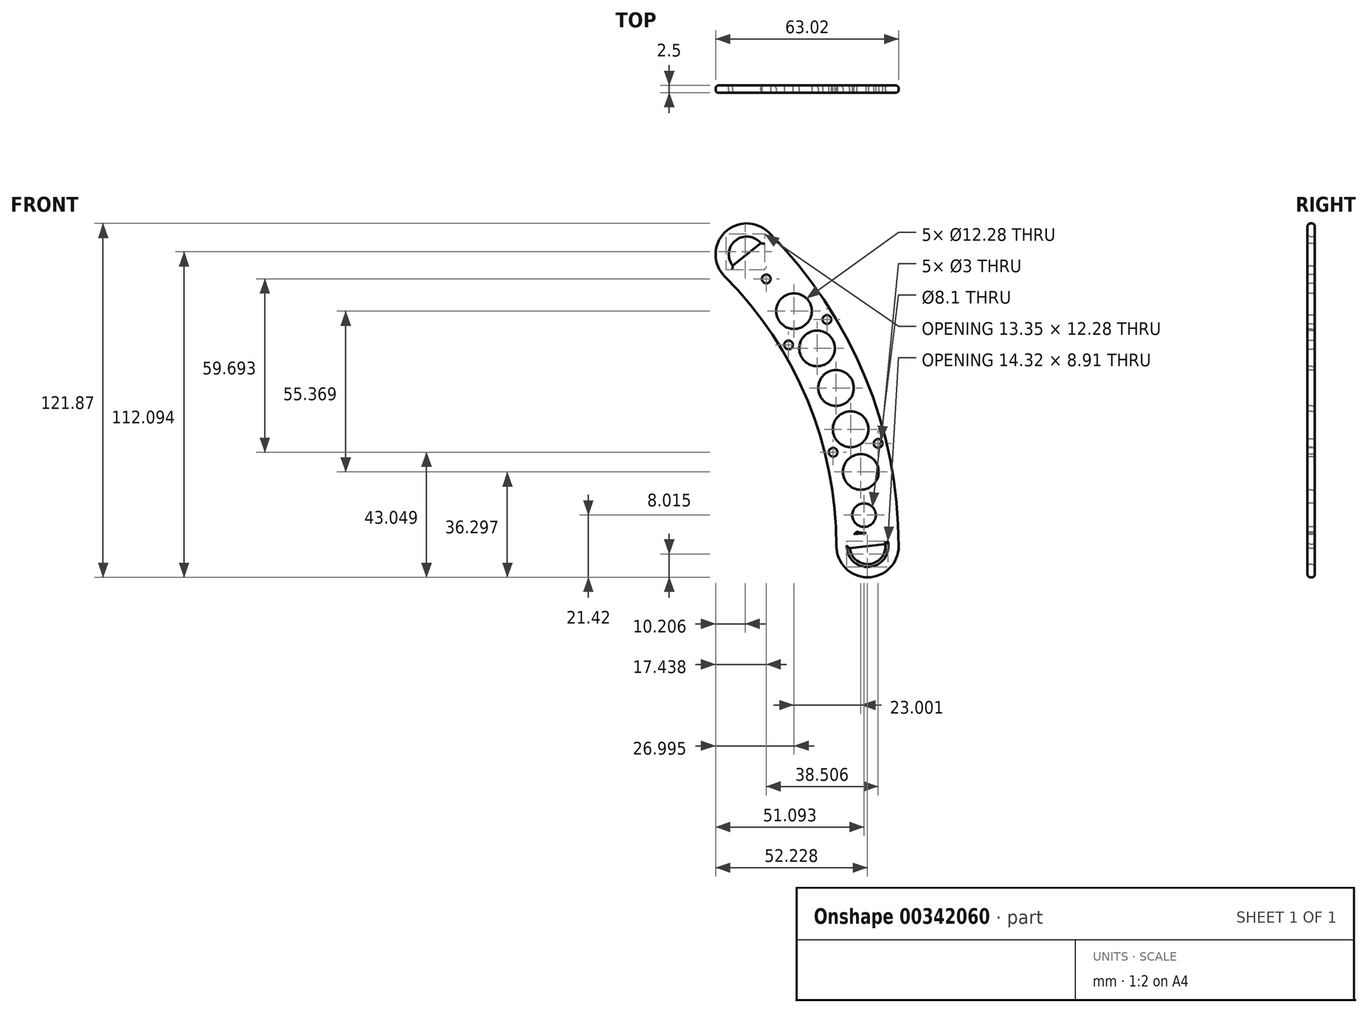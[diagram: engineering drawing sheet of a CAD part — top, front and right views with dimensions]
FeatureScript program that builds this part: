
annotation { "Feature Type Name" : "Feature", "Feature Type Description" : "" }
export const myFeature = defineFeature(function(context is Context, id is Id, definition is map)
    precondition{}
    {
        {
            var Q0;
            Q0=qCreatedBy(makeId("Front.planeOp"),FACE);
            var sketch = newSketch(context, id + "F0", { "sketchPlane" : qUnion([Q0])});
            skCircle(sketch, "E0", {"center": v(0, 0) * mm, "radius": 152.8 * mm});
            skCircle(sketch, "E1", {"center": v(0, 0) * mm, "radius": 131.4 * mm});
            skLineSegment(sketch, "E2", {"start": v(0, 0) * mm, "end": v(152.8, 0) * mm, "construction": true});
            skLineSegment(sketch, "E3", {"start": v(0, 0) * mm, "end": v(108.04, 108.04) * mm, "construction": true});
            skPoint(sketch, "E4", {"position": v(92.9, 92.9) * mm});
            skPoint(sketch, "E5", {"position": v(108.04, 108.04) * mm});
            skPoint(sketch, "E6", {"position": v(131.4, 0) * mm});
            skPoint(sketch, "E7", {"position": v(152.8, 0) * mm});
            skCircle(sketch, "E8", {"center": v(100.47, 100.47) * mm, "radius": 10.7 * mm});
            skCircle(sketch, "E9", {"center": v(142.1, 0) * mm, "radius": 10.7 * mm});
            skLineSegment(sketch, "E10", {"start": v(142.1, 0) * mm, "end": v(148.23, 0.7) * mm});
            skLineSegment(sketch, "E11", {"start": v(142.1, 0) * mm, "end": v(135.94, -0.7) * mm});
            skLineSegment(sketch, "E12", {"start": v(148.23, 0.7) * mm, "end": v(144.58, 32.71) * mm});
            skLineSegment(sketch, "E13", {"start": v(135.94, -0.7) * mm, "end": v(132.3, 31.31) * mm});
            skLineSegment(sketch, "E14", {"start": v(132.3, 31.31) * mm, "end": v(144.58, 32.71) * mm});
            skLineSegment(sketch, "E15", {"start": v(100.47, 100.47) * mm, "end": v(105.3, 104.33) * mm});
            skLineSegment(sketch, "E16", {"start": v(100.47, 100.47) * mm, "end": v(95.64, 96.62) * mm});
            skLineSegment(sketch, "E17", {"start": v(120.53, 75.25) * mm, "end": v(125.41, 79.16) * mm});
            skLineSegment(sketch, "E18", {"start": v(120.53, 75.25) * mm, "end": v(115.75, 71.44) * mm});
            skLineSegment(sketch, "E19", {"start": v(105.3, 104.33) * mm, "end": v(125.41, 79.16) * mm});
            skLineSegment(sketch, "E20", {"start": v(95.64, 96.62) * mm, "end": v(115.75, 71.44) * mm});
            skLineSegment(sketch, "E21", {"start": v(135.42, 3.88) * mm, "end": v(147.7, 5.28) * mm});
            skLineSegment(sketch, "E22", {"start": v(132.82, 26.73) * mm, "end": v(145.1, 28.13) * mm});
            skLineSegment(sketch, "E23", {"start": v(112.88, 75.04) * mm, "end": v(122.53, 82.76) * mm});
            skLineSegment(sketch, "E24", {"start": v(98.52, 93.01) * mm, "end": v(108.18, 100.73) * mm});
            skCircle(sketch, "E25", {"center": v(0, 0) * mm, "radius": 148.23 * mm, "construction": true});
            skCircle(sketch, "E26", {"center": v(0, 0) * mm, "radius": 135.95 * mm, "construction": true});
            skCircle(sketch, "E27", {"center": v(141.82, 2.29) * mm, "radius": 1 * mm});
            skCircle(sketch, "E28", {"center": v(138.7, 29.72) * mm, "radius": 1 * mm});
            skCircle(sketch, "E29", {"center": v(140.86, 10.72) * mm, "radius": 6.18 * mm});
            skLineSegment(sketch, "E30", {"start": v(122.53, 82.76) * mm, "end": v(115.75, 71.44) * mm, "construction": true});
            skLineSegment(sketch, "E31", {"start": v(112.88, 75.04) * mm, "end": v(125.41, 79.16) * mm, "construction": true});
            skCircle(sketch, "E32", {"center": v(101.91, 98.67) * mm, "radius": 1 * mm});
            skCircle(sketch, "E33", {"center": v(119.14, 77.1) * mm, "radius": 1 * mm});
            skCircle(sketch, "E34", {"center": v(107.2, 92.04) * mm, "radius": 6.18 * mm});
            skLineSegment(sketch, "E35", {"start": v(132.82, 26.73) * mm, "end": v(144.58, 32.71) * mm, "construction": true});
            skLineSegment(sketch, "E36", {"start": v(145.1, 28.13) * mm, "end": v(132.3, 31.31) * mm, "construction": true});
            skCircle(sketch, "E37", {"center": v(100.47, 100.47) * mm, "radius": 6.18 * mm});
            skCircle(sketch, "E38", {"center": v(142.1, 0) * mm, "radius": 6.19 * mm});
            skLineSegment(sketch, "E39", {"start": v(135.42, 3.88) * mm, "end": v(148.23, 0.7) * mm, "construction": true});
            skLineSegment(sketch, "E40", {"start": v(135.94, -0.7) * mm, "end": v(147.7, 5.28) * mm, "construction": true});
            skLineSegment(sketch, "E41", {"start": v(148.23, 0.7) * mm, "end": v(148.24, 0.7) * mm});
            skSolve(sketch);
        }
        {
            var Q0;
            {var subQ16=sQuery(id+"F0.wireOp",EDGE,"E18");Q0=makeQuery(id+"F0.imprint","IMPRINT",FACE,{"disambiguationData":[TD([[makeQuery(id+"F0.imprint","IMPRINT",EDGE,{"derivedFrom":subQ16}),1.0]])]});}
            var Q1;
            {var subQ14=sQuery(id+"F0.wireOp",EDGE,"E17");Q1=makeQuery(id+"F0.imprint","IMPRINT",FACE,{"disambiguationData":[TD([[makeQuery(id+"F0.imprint","IMPRINT",EDGE,{"derivedFrom":subQ14}),-1.0]])]});}
            var Q2;
            {var subQ3=sQuery(id+"F0.wireOp",EDGE,"oQQra7B9-EMDj-B2YQ-GpEd-beqhVWcHA2Qh");var subQ5=sQuery(id+"F0.wireOp",EDGE,"E22");var subQ9=makeQuery(id+"F0.imprint","INTERSECT",VERTEX,{"derivedFrom":[subQ3,subQ5]});Q2=makeQuery(id+"F0.imprint","IMPRINT",FACE,{"disambiguationData":[TD([[makeQuery(id+"F0.imprint","IMPRINT",EDGE,{"disambiguationData":[TD([[subQ9,-1.0]])],"derivedFrom":subQ3}),-1.0]])]});}
            var Q3;
            {var subQ3=sQuery(id+"F0.wireOp",EDGE,"oQQra7B9-EMDj-B2YQ-GpEd-beqhVWcHA2Qh");var subQ5=sQuery(id+"F0.wireOp",EDGE,"E22");var subQ9=makeQuery(id+"F0.imprint","INTERSECT",VERTEX,{"derivedFrom":[subQ3,subQ5]});Q3=makeQuery(id+"F0.imprint","IMPRINT",FACE,{"disambiguationData":[TD([[makeQuery(id+"F0.imprint","IMPRINT",EDGE,{"disambiguationData":[TD([[subQ9,-1.0]])],"derivedFrom":subQ3}),1.0]])]});}
            var Q4;
            {var subQ5=sQuery(id+"F0.wireOp",EDGE,"E9");var subQ8=makeQuery(id+"F0.imprint","INTERSECT",VERTEX,{"derivedFrom":[sQuery(id+"F0.wireOp",EDGE,"E1"),subQ5]});Q4=makeQuery(id+"F0.imprint","IMPRINT",FACE,{"disambiguationData":[TD([[makeQuery(id+"F0.imprint","IMPRINT",EDGE,{"disambiguationData":[TD([[subQ8,1.0]])],"derivedFrom":subQ5}),1.0]])]});}
            var Q5;
            {var subQ1=sQuery(id+"F0.wireOp",EDGE,"E9");var subQ5=makeQuery(id+"F0.imprint","INTERSECT",VERTEX,{"derivedFrom":[sQuery(id+"F0.wireOp",EDGE,"E0"),subQ1]});Q5=makeQuery(id+"F0.imprint","IMPRINT",FACE,{"disambiguationData":[TD([[makeQuery(id+"F0.imprint","IMPRINT",EDGE,{"disambiguationData":[TD([[subQ5,-1.0]])],"derivedFrom":subQ1}),1.0]])]});}
            var Q6;
            {var subQ1=sQuery(id+"F0.wireOp",EDGE,"E13");var subQ3=sQuery(id+"F0.wireOp",EDGE,"E21");var subQ4=makeQuery(id+"F0.imprint","INTERSECT",VERTEX,{"derivedFrom":[subQ1,subQ3]});Q6=makeQuery(id+"F0.imprint","IMPRINT",FACE,{"disambiguationData":[TD([[makeQuery(id+"F0.imprint","IMPRINT",EDGE,{"disambiguationData":[TD([[subQ4,-1.0]])],"derivedFrom":subQ3}),-1.0]])]});}
            var Q7;
            {var subQ1=sQuery(id+"F0.wireOp",EDGE,"E12");var subQ3=sQuery(id+"F0.wireOp",EDGE,"E21");var subQ4=makeQuery(id+"F0.imprint","INTERSECT",VERTEX,{"derivedFrom":[subQ1,subQ3]});Q7=makeQuery(id+"F0.imprint","IMPRINT",FACE,{"disambiguationData":[TD([[makeQuery(id+"F0.imprint","IMPRINT",EDGE,{"disambiguationData":[TD([[subQ4,1.0]])],"derivedFrom":subQ3}),-1.0]])]});}
            var Q8;
            {var subQ4=sQuery(id+"F0.wireOp",EDGE,"E8");var subQ5=makeQuery(id+"F0.imprint","INTERSECT",VERTEX,{"derivedFrom":[sQuery(id+"F0.wireOp",EDGE,"E0"),subQ4]});Q8=makeQuery(id+"F0.imprint","IMPRINT",FACE,{"disambiguationData":[TD([[makeQuery(id+"F0.imprint","IMPRINT",EDGE,{"disambiguationData":[TD([[subQ5,-1.0]])],"derivedFrom":subQ4}),1.0]])]});}
            var Q9;
            {var subQ5=sQuery(id+"F0.wireOp",EDGE,"E8");var subQ9=makeQuery(id+"F0.imprint","INTERSECT",VERTEX,{"derivedFrom":[sQuery(id+"F0.wireOp",EDGE,"E1"),subQ5]});Q9=makeQuery(id+"F0.imprint","IMPRINT",FACE,{"disambiguationData":[TD([[makeQuery(id+"F0.imprint","IMPRINT",EDGE,{"disambiguationData":[TD([[subQ9,1.0]])],"derivedFrom":subQ5}),1.0]])]});}
            var Q10;
            {var subQ1=sQuery(id+"F0.wireOp",EDGE,"E20");var subQ3=sQuery(id+"F0.wireOp",EDGE,"E24");var subQ4=makeQuery(id+"F0.imprint","INTERSECT",VERTEX,{"derivedFrom":[subQ1,subQ3]});Q10=makeQuery(id+"F0.imprint","IMPRINT",FACE,{"disambiguationData":[TD([[makeQuery(id+"F0.imprint","IMPRINT",EDGE,{"disambiguationData":[TD([[subQ4,-1.0]])],"derivedFrom":subQ3}),1.0]])]});}
            var Q11;
            {var subQ4=sQuery(id+"F0.wireOp",EDGE,"E16");Q11=makeQuery(id+"F0.imprint","IMPRINT",FACE,{"disambiguationData":[TD([[makeQuery(id+"F0.imprint","IMPRINT",EDGE,{"derivedFrom":subQ4}),1.0]])]});}
            var Q12;
            {var subQ0=sQuery(id+"F0.wireOp",EDGE,"E15");Q12=makeQuery(id+"F0.imprint","IMPRINT",FACE,{"disambiguationData":[TD([[makeQuery(id+"F0.imprint","IMPRINT",EDGE,{"derivedFrom":subQ0}),-1.0]])]});}
            var Q13;
            {var subQ1=sQuery(id+"F0.wireOp",EDGE,"E19");var subQ3=sQuery(id+"F0.wireOp",EDGE,"E24");var subQ4=makeQuery(id+"F0.imprint","INTERSECT",VERTEX,{"derivedFrom":[subQ1,subQ3]});Q13=makeQuery(id+"F0.imprint","IMPRINT",FACE,{"disambiguationData":[TD([[makeQuery(id+"F0.imprint","IMPRINT",EDGE,{"disambiguationData":[TD([[subQ4,1.0]])],"derivedFrom":subQ3}),1.0]])]});}
            var Q14;
            {var subQ1=sQuery(id+"F0.wireOp",EDGE,"E18");Q14=makeQuery(id+"F0.imprint","IMPRINT",FACE,{"disambiguationData":[TD([[makeQuery(id+"F0.imprint","IMPRINT",EDGE,{"derivedFrom":subQ1}),-1.0]])]});}
            var Q15;
            {var subQ1=sQuery(id+"F0.wireOp",EDGE,"E17");Q15=makeQuery(id+"F0.imprint","IMPRINT",FACE,{"disambiguationData":[TD([[makeQuery(id+"F0.imprint","IMPRINT",EDGE,{"derivedFrom":subQ1}),1.0]])]});}
            var Q16;
            {var subQ0=sQuery(id+"F0.wireOp",EDGE,"E14");Q16=makeQuery(id+"F0.imprint","IMPRINT",FACE,{"disambiguationData":[TD([[makeQuery(id+"F0.imprint","IMPRINT",EDGE,{"derivedFrom":subQ0}),-1.0]])]});}
            var Q17;
            {var subQ5=sQuery(id+"F0.wireOp",EDGE,"E10");Q17=makeQuery(id+"F0.imprint","IMPRINT",FACE,{"disambiguationData":[TD([[makeQuery(id+"F0.imprint","IMPRINT",EDGE,{"derivedFrom":subQ5}),1.0]])]});}
            var Q18;
            Q18=makeQuery(id+"F0.imprint","IMPRINT",FACE,{"disambiguationData":[TD([[makeQuery(id+"F0.imprint","IMPRINT",EDGE,{"derivedFrom":sQuery(id+"F0.wireOp",EDGE,"E27")}),-1.0]])]});
            var Q19;
            {var subQ0=sQuery(id+"F0.wireOp",EDGE,"E41");Q19=makeQuery(id+"F0.imprint","IMPRINT",FACE,{"disambiguationData":[TD([[makeQuery(id+"F0.imprint","IMPRINT",EDGE,{"derivedFrom":subQ0}),1.0]])]});}
            extrude(context, id + "F1", {"entities" : qUnion([Q0, Q1, Q2, Q3, Q4, Q5, Q6, Q7, Q8, Q9, Q10, Q11, Q12, Q13, Q14, Q15, Q16, Q17, Q18, Q19]), "depth" : 2.5 * mm});
        }
        {
            var Q0;
            Q0=makeQuery(id+"F1.opExtrude","CAP_FACE",FACE,{"disambiguationData":[OSD([sQuery(id+"F0.wireOp",EDGE,"E0"),sQuery(id+"F0.wireOp",EDGE,"E1"),sQuery(id+"F0.wireOp",EDGE,"E8"),sQuery(id+"F0.wireOp",EDGE,"E9"),sQuery(id+"F0.wireOp",EDGE,"E10"),sQuery(id+"F0.wireOp",EDGE,"E11"),sQuery(id+"F0.wireOp",EDGE,"E12"),sQuery(id+"F0.wireOp",EDGE,"E13"),sQuery(id+"F0.wireOp",EDGE,"E15"),sQuery(id+"F0.wireOp",EDGE,"E16"),sQuery(id+"F0.wireOp",EDGE,"E19"),sQuery(id+"F0.wireOp",EDGE,"E20"),sQuery(id+"F0.wireOp",EDGE,"E21"),sQuery(id+"F0.wireOp",EDGE,"E22"),sQuery(id+"F0.wireOp",EDGE,"E23"),sQuery(id+"F0.wireOp",EDGE,"E24"),sQuery(id+"F0.wireOp",EDGE,"E27"),sQuery(id+"F0.wireOp",EDGE,"E28"),sQuery(id+"F0.wireOp",EDGE,"E32"),sQuery(id+"F0.wireOp",EDGE,"E33"),sQuery(id+"F0.wireOp",EDGE,"E37"),sQuery(id+"F0.wireOp",EDGE,"E38")])],"isStart":false});
            var sketch = newSketch(context, id + "F2", { "sketchPlane" : qUnion([Q0])});
            skCircle(sketch, "E42", {"center": v(136.26, 40.28) * mm, "radius": 6.14 * mm});
            skCircle(sketch, "E43", {"center": v(124.7, 68.12) * mm, "radius": 6.14 * mm});
            skCircle(sketch, "E44", {"center": v(131.22, 54.5) * mm, "radius": 6.14 * mm});
            skCircle(sketch, "E45", {"center": v(0, 0) * mm, "radius": 142.1 * mm, "construction": true});
            skLineSegment(sketch, "E46", {"start": v(0, 0) * mm, "end": v(136.26, 40.28) * mm, "construction": true});
            skLineSegment(sketch, "E47", {"start": v(0, 0) * mm, "end": v(131.22, 54.5) * mm, "construction": true});
            skLineSegment(sketch, "E48", {"start": v(0, 0) * mm, "end": v(124.7, 68.12) * mm, "construction": true});
            skCircle(sketch, "E49", {"center": v(0, 0) * mm, "radius": 152.8 * mm, "construction": true});
            skCircle(sketch, "E50", {"center": v(0, 0) * mm, "radius": 131.4 * mm, "construction": true});
            skCircle(sketch, "E51", {"center": v(0, 0) * mm, "radius": 135.95 * mm, "construction": true});
            skCircle(sketch, "E52", {"center": v(0, 0) * mm, "radius": 148.23 * mm, "construction": true});
            skLineSegment(sketch, "E53", {"start": v(112.88, 75.04) * mm, "end": v(119.3, 65.18) * mm, "construction": true});
            skLineSegment(sketch, "E54", {"start": v(119.3, 65.18) * mm, "end": v(118, 79.14) * mm, "construction": true});
            skLineSegment(sketch, "E55", {"start": v(118, 79.14) * mm, "end": v(130.08, 71.07) * mm, "construction": true});
            skLineSegment(sketch, "E56", {"start": v(130.08, 71.07) * mm, "end": v(122.53, 82.76) * mm, "construction": true});
            skLineSegment(sketch, "E57", {"start": v(122.53, 82.76) * mm, "end": v(118, 79.14) * mm});
            skLineSegment(sketch, "E58", {"start": v(112.88, 75.04) * mm, "end": v(118, 79.14) * mm});
            skLineSegment(sketch, "E59", {"start": v(126.3, 76.91) * mm, "end": v(130.43, 79.57) * mm, "construction": true});
            skCircle(sketch, "E60", {"center": v(128.1, 78.07) * mm, "radius": 1 * mm});
            skLineSegment(sketch, "E61", {"start": v(130.37, 38.54) * mm, "end": v(132.82, 26.73) * mm});
            skLineSegment(sketch, "E62", {"start": v(145.1, 28.13) * mm, "end": v(142.22, 41.78) * mm});
            skLineSegment(sketch, "E63", {"start": v(131.6, 32.64) * mm, "end": v(127.49, 31.79) * mm});
            skLineSegment(sketch, "E64", {"start": v(143.66, 34.96) * mm, "end": v(148.5, 35.98) * mm});
            skCircle(sketch, "E65", {"center": v(130.21, 32.35) * mm, "radius": 1 * mm});
            skCircle(sketch, "E66", {"center": v(145.71, 35.4) * mm, "radius": 1 * mm});
            skLineSegment(sketch, "E67", {"start": v(116.1, 70.11) * mm, "end": v(112.55, 67.8) * mm, "construction": true});
            skCircle(sketch, "E68", {"center": v(114.87, 69.32) * mm, "radius": 1 * mm});
            skLineSegment(sketch, "E69", {"start": v(0, 0) * mm, "end": v(116.76, 80.97) * mm, "construction": true});
            skLineSegment(sketch, "E70", {"start": v(0, 0) * mm, "end": v(139.77, 25.6) * mm, "construction": true});
            skCircle(sketch, "E71", {"center": v(139.77, 25.6) * mm, "radius": 6.14 * mm});
            skCircle(sketch, "E72", {"center": v(116.76, 80.97) * mm, "radius": 6.14 * mm});
            skSolve(sketch);
        }
        {
            var Q0;
            Q0=makeQuery(id+"F2.imprint","IMPRINT",FACE,{"disambiguationData":[TD([[makeQuery(id+"F2.imprint","IMPRINT",EDGE,{"derivedFrom":sQuery(id+"F2.wireOp",EDGE,"E43")}),1.0]])]});
            var Q1;
            Q1=makeQuery(id+"F2.imprint","IMPRINT",FACE,{"disambiguationData":[TD([[makeQuery(id+"F2.imprint","IMPRINT",EDGE,{"derivedFrom":sQuery(id+"F2.wireOp",EDGE,"E44")}),1.0]])]});
            var Q2;
            Q2=makeQuery(id+"F2.imprint","IMPRINT",FACE,{"disambiguationData":[TD([[makeQuery(id+"F2.imprint","IMPRINT",EDGE,{"derivedFrom":sQuery(id+"F2.wireOp",EDGE,"E42")}),1.0]])]});
            var Q3;
            {var subQ0=sQuery(id+"F2.wireOp",EDGE,"E56");var subQ1=sQuery(id+"F2.wireOp",EDGE,"E43");var subQ2=makeQuery(id+"F2.imprint","INTERSECT",VERTEX,{"derivedFrom":[subQ1,subQ0]});Q3=makeQuery(id+"F2.imprint","IMPRINT",FACE,{"disambiguationData":[TD([[makeQuery(id+"F2.imprint","IMPRINT",EDGE,{"disambiguationData":[TD([[subQ2,-1.0]])],"derivedFrom":subQ1}),1.0]])]});}
            var Q4;
            {var subQ0=sQuery(id+"F2.wireOp",EDGE,"E54");var subQ1=sQuery(id+"F2.wireOp",EDGE,"E43");var subQ3=makeQuery(id+"F2.imprint","INTERSECT",VERTEX,{"derivedFrom":[subQ1,subQ0]});Q4=makeQuery(id+"F2.imprint","IMPRINT",FACE,{"disambiguationData":[TD([[makeQuery(id+"F2.imprint","IMPRINT",EDGE,{"disambiguationData":[TD([[subQ3,-1.0]])],"derivedFrom":subQ1}),1.0]])]});}
            var Q5;
            Q5=makeQuery(id+"F2.imprint","IMPRINT",FACE,{"disambiguationData":[TD([[makeQuery(id+"F2.imprint","IMPRINT",EDGE,{"derivedFrom":sQuery(id+"F2.wireOp",EDGE,"6Q9i7ZKX-M5Zn-dDvE-S5ua-DKoOSJd4rO0q")}),1.0]])]});
            var Q6;
            Q6=makeQuery(id+"F2.imprint","IMPRINT",FACE,{"disambiguationData":[TD([[makeQuery(id+"F2.imprint","IMPRINT",EDGE,{"derivedFrom":sQuery(id+"F2.wireOp",EDGE,"E60")}),1.0]])]});
            var Q7;
            Q7=makeQuery(id+"F2.imprint","IMPRINT",FACE,{"disambiguationData":[TD([[makeQuery(id+"F2.imprint","IMPRINT",EDGE,{"derivedFrom":sQuery(id+"F2.wireOp",EDGE,"E68")}),1.0]])]});
            var Q8;
            {var subQ0=sQuery(id+"F2.wireOp",EDGE,"E66");var subQ1=sQuery(id+"F2.wireOp",EDGE,"E64");var subQ2=makeQuery(id+"F2.imprint","INTERSECT",VERTEX,{"disambiguationData":[OD(0.0)],"derivedFrom":[subQ1,subQ0]});Q8=makeQuery(id+"F2.imprint","IMPRINT",FACE,{"disambiguationData":[TD([[makeQuery(id+"F2.imprint","IMPRINT",EDGE,{"disambiguationData":[TD([[subQ2,-1.0]])],"derivedFrom":subQ1}),1.0]])]});}
            var Q9;
            {var subQ0=sQuery(id+"F2.wireOp",EDGE,"E66");var subQ1=sQuery(id+"F2.wireOp",EDGE,"E64");var subQ2=makeQuery(id+"F2.imprint","INTERSECT",VERTEX,{"disambiguationData":[OD(0.0)],"derivedFrom":[subQ1,subQ0]});Q9=makeQuery(id+"F2.imprint","IMPRINT",FACE,{"disambiguationData":[TD([[makeQuery(id+"F2.imprint","IMPRINT",EDGE,{"disambiguationData":[TD([[subQ2,-1.0]])],"derivedFrom":subQ1}),-1.0]])]});}
            var Q10;
            {var subQ0=sQuery(id+"F2.wireOp",EDGE,"E65");var subQ1=sQuery(id+"F2.wireOp",EDGE,"E63");var subQ2=makeQuery(id+"F2.imprint","INTERSECT",VERTEX,{"disambiguationData":[OD(0.0)],"derivedFrom":[subQ1,subQ0]});Q10=makeQuery(id+"F2.imprint","IMPRINT",FACE,{"disambiguationData":[TD([[makeQuery(id+"F2.imprint","IMPRINT",EDGE,{"disambiguationData":[TD([[subQ2,-1.0]])],"derivedFrom":subQ1}),1.0]])]});}
            var Q11;
            {var subQ0=sQuery(id+"F2.wireOp",EDGE,"E65");var subQ1=sQuery(id+"F2.wireOp",EDGE,"E63");var subQ2=makeQuery(id+"F2.imprint","INTERSECT",VERTEX,{"disambiguationData":[OD(0.0)],"derivedFrom":[subQ1,subQ0]});Q11=makeQuery(id+"F2.imprint","IMPRINT",FACE,{"disambiguationData":[TD([[makeQuery(id+"F2.imprint","IMPRINT",EDGE,{"disambiguationData":[TD([[subQ2,-1.0]])],"derivedFrom":subQ1}),-1.0]])]});}
            extrude(context, id + "F3", {"entities" : qUnion([Q0, Q1, Q2, Q3, Q4, Q5, Q6, Q7, Q8, Q9, Q10, Q11]), "operationType" : NewBodyOperationType.REMOVE, "oppositeDirection" : true, "depth" : 25 * mm});
        }
        {
            var Q0;
            {var subQ1=sQuery(id+"F0.wireOp",EDGE,"E9");var subQ6=sQuery(id+"F0.wireOp",EDGE,"E12");var subQ8=makeQuery(id+"F0.imprint","INTERSECT",VERTEX,{"derivedFrom":[subQ1,subQ6]});Q0=makeQuery(id+"F0.imprint","IMPRINT",FACE,{"disambiguationData":[TD([[makeQuery(id+"F0.imprint","IMPRINT",EDGE,{"disambiguationData":[TD([[subQ8,-1.0]])],"derivedFrom":subQ1}),1.0]])]});}
            var Q1;
            {var subQ0=sQuery(id+"F0.wireOp",EDGE,"E29");var subQ1=sQuery(id+"F0.wireOp",EDGE,"E9");var subQ2=makeQuery(id+"F0.imprint","INTERSECT",VERTEX,{"disambiguationData":[OD(0.0)],"derivedFrom":[subQ1,subQ0]});Q1=makeQuery(id+"F0.imprint","IMPRINT",FACE,{"disambiguationData":[TD([[makeQuery(id+"F0.imprint","IMPRINT",EDGE,{"disambiguationData":[TD([[subQ2,-1.0]])],"derivedFrom":subQ1}),-1.0]])]});}
            var Q2;
            {var subQ0=sQuery(id+"F0.wireOp",EDGE,"E29");var subQ1=sQuery(id+"F0.wireOp",EDGE,"E9");var subQ2=makeQuery(id+"F0.imprint","INTERSECT",VERTEX,{"disambiguationData":[OD(0.0)],"derivedFrom":[subQ1,subQ0]});Q2=makeQuery(id+"F0.imprint","IMPRINT",FACE,{"disambiguationData":[TD([[makeQuery(id+"F0.imprint","IMPRINT",EDGE,{"disambiguationData":[TD([[subQ2,-1.0]])],"derivedFrom":subQ1}),1.0]])]});}
            var Q3;
            {var subQ0=sQuery(id+"F0.wireOp",EDGE,"E29");var subQ1=makeQuery(id+"F0.imprint","INTERSECT",VERTEX,{"derivedFrom":[sQuery(id+"F0.wireOp",EDGE,"E21"),subQ0]});Q3=makeQuery(id+"F0.imprint","IMPRINT",FACE,{"disambiguationData":[TD([[makeQuery(id+"F0.imprint","IMPRINT",EDGE,{"disambiguationData":[TD([[subQ1,1.0]])],"derivedFrom":subQ0}),1.0]])]});}
            var Q4;
            {var subQ0=sQuery(id+"F0.wireOp",EDGE,"E29");var subQ1=sQuery(id+"F0.wireOp",EDGE,"E9");var subQ2=makeQuery(id+"F0.imprint","INTERSECT",VERTEX,{"disambiguationData":[OD(1.0)],"derivedFrom":[subQ1,subQ0]});Q4=makeQuery(id+"F0.imprint","IMPRINT",FACE,{"disambiguationData":[TD([[makeQuery(id+"F0.imprint","IMPRINT",EDGE,{"disambiguationData":[TD([[subQ2,-1.0]])],"derivedFrom":subQ1}),1.0]])]});}
            var Q5;
            {var subQ0=sQuery(id+"F0.wireOp",EDGE,"E38");var subQ1=sQuery(id+"F0.wireOp",EDGE,"E21");var subQ2=makeQuery(id+"F0.imprint","INTERSECT",VERTEX,{"disambiguationData":[OD(0.0)],"derivedFrom":[subQ1,subQ0]});Q5=makeQuery(id+"F0.imprint","IMPRINT",FACE,{"disambiguationData":[TD([[makeQuery(id+"F0.imprint","IMPRINT",EDGE,{"disambiguationData":[TD([[subQ2,-1.0]])],"derivedFrom":subQ1}),1.0]])]});}
            var Q6;
            {var subQ0=sQuery(id+"F0.wireOp",EDGE,"E29");var subQ1=sQuery(id+"F0.wireOp",EDGE,"E21");var subQ2=makeQuery(id+"F0.imprint","INTERSECT",VERTEX,{"derivedFrom":[subQ1,subQ0]});Q6=makeQuery(id+"F0.imprint","IMPRINT",FACE,{"disambiguationData":[TD([[makeQuery(id+"F0.imprint","IMPRINT",EDGE,{"disambiguationData":[TD([[subQ2,-1.0]])],"derivedFrom":subQ1}),1.0]])]});}
            var Q7;
            {var subQ0=sQuery(id+"F0.wireOp",EDGE,"E22");Q7=makeQuery(id+"F0.imprint","IMPRINT",FACE,{"disambiguationData":[TD([[makeQuery(id+"F0.imprint","IMPRINT",EDGE,{"derivedFrom":subQ0}),-1.0]])]});}
            var Q8;
            {var subQ0=sQuery(id+"F0.wireOp",EDGE,"E12");var subQ1=sQuery(id+"F0.wireOp",EDGE,"E9");var subQ2=makeQuery(id+"F0.imprint","INTERSECT",VERTEX,{"derivedFrom":[subQ1,subQ0]});Q8=makeQuery(id+"F0.imprint","IMPRINT",FACE,{"disambiguationData":[TD([[makeQuery(id+"F0.imprint","IMPRINT",EDGE,{"disambiguationData":[TD([[subQ2,-1.0]])],"derivedFrom":subQ1}),-1.0]])]});}
            var Q9;
            {var subQ0=sQuery(id+"F0.wireOp",EDGE,"E29");var subQ1=sQuery(id+"F0.wireOp",EDGE,"E9");var subQ2=makeQuery(id+"F0.imprint","INTERSECT",VERTEX,{"disambiguationData":[OD(1.0)],"derivedFrom":[subQ1,subQ0]});Q9=makeQuery(id+"F0.imprint","IMPRINT",FACE,{"disambiguationData":[TD([[makeQuery(id+"F0.imprint","IMPRINT",EDGE,{"disambiguationData":[TD([[subQ2,-1.0]])],"derivedFrom":subQ1}),-1.0]])]});}
            var Q10;
            {var subQ0=sQuery(id+"F0.wireOp",EDGE,"E23");Q10=makeQuery(id+"F0.imprint","IMPRINT",FACE,{"disambiguationData":[TD([[makeQuery(id+"F0.imprint","IMPRINT",EDGE,{"derivedFrom":subQ0}),1.0]])]});}
            var Q11;
            {var subQ0=sQuery(id+"F0.wireOp",EDGE,"E34");var subQ1=sQuery(id+"F0.wireOp",EDGE,"E8");var subQ2=makeQuery(id+"F0.imprint","INTERSECT",VERTEX,{"disambiguationData":[OD(0.0)],"derivedFrom":[subQ1,subQ0]});Q11=makeQuery(id+"F0.imprint","IMPRINT",FACE,{"disambiguationData":[TD([[makeQuery(id+"F0.imprint","IMPRINT",EDGE,{"disambiguationData":[TD([[subQ2,-1.0]])],"derivedFrom":subQ1}),-1.0]])]});}
            var Q12;
            {var subQ0=sQuery(id+"F0.wireOp",EDGE,"E34");var subQ1=sQuery(id+"F0.wireOp",EDGE,"E8");var subQ2=makeQuery(id+"F0.imprint","INTERSECT",VERTEX,{"disambiguationData":[OD(0.0)],"derivedFrom":[subQ1,subQ0]});Q12=makeQuery(id+"F0.imprint","IMPRINT",FACE,{"disambiguationData":[TD([[makeQuery(id+"F0.imprint","IMPRINT",EDGE,{"disambiguationData":[TD([[subQ2,-1.0]])],"derivedFrom":subQ1}),1.0]])]});}
            var Q13;
            {var subQ0=sQuery(id+"F0.wireOp",EDGE,"E34");var subQ1=sQuery(id+"F0.wireOp",EDGE,"E8");var subQ2=makeQuery(id+"F0.imprint","INTERSECT",VERTEX,{"disambiguationData":[OD(1.0)],"derivedFrom":[subQ1,subQ0]});Q13=makeQuery(id+"F0.imprint","IMPRINT",FACE,{"disambiguationData":[TD([[makeQuery(id+"F0.imprint","IMPRINT",EDGE,{"disambiguationData":[TD([[subQ2,-1.0]])],"derivedFrom":subQ1}),1.0]])]});}
            var Q14;
            {var subQ0=sQuery(id+"F0.wireOp",EDGE,"E34");var subQ1=sQuery(id+"F0.wireOp",EDGE,"E24");var subQ2=makeQuery(id+"F0.imprint","INTERSECT",VERTEX,{"derivedFrom":[subQ1,subQ0]});Q14=makeQuery(id+"F0.imprint","IMPRINT",FACE,{"disambiguationData":[TD([[makeQuery(id+"F0.imprint","IMPRINT",EDGE,{"disambiguationData":[TD([[subQ2,-1.0]])],"derivedFrom":subQ1}),-1.0]])]});}
            var Q15;
            {var subQ0=sQuery(id+"F0.wireOp",EDGE,"E34");var subQ1=makeQuery(id+"F0.imprint","INTERSECT",VERTEX,{"derivedFrom":[sQuery(id+"F0.wireOp",EDGE,"E24"),subQ0]});Q15=makeQuery(id+"F0.imprint","IMPRINT",FACE,{"disambiguationData":[TD([[makeQuery(id+"F0.imprint","IMPRINT",EDGE,{"disambiguationData":[TD([[subQ1,1.0]])],"derivedFrom":subQ0}),1.0]])]});}
            var Q16;
            {var subQ0=sQuery(id+"F0.wireOp",EDGE,"E37");var subQ1=sQuery(id+"F0.wireOp",EDGE,"E24");var subQ2=makeQuery(id+"F0.imprint","INTERSECT",VERTEX,{"disambiguationData":[OD(0.0)],"derivedFrom":[subQ1,subQ0]});Q16=makeQuery(id+"F0.imprint","IMPRINT",FACE,{"disambiguationData":[TD([[makeQuery(id+"F0.imprint","IMPRINT",EDGE,{"disambiguationData":[TD([[subQ2,-1.0]])],"derivedFrom":subQ1}),-1.0]])]});}
            var Q17;
            {var subQ1=sQuery(id+"F0.wireOp",EDGE,"E8");var subQ6=sQuery(id+"F0.wireOp",EDGE,"E20");var subQ9=makeQuery(id+"F0.imprint","INTERSECT",VERTEX,{"derivedFrom":[subQ1,subQ6]});Q17=makeQuery(id+"F0.imprint","IMPRINT",FACE,{"disambiguationData":[TD([[makeQuery(id+"F0.imprint","IMPRINT",EDGE,{"disambiguationData":[TD([[subQ9,-1.0]])],"derivedFrom":subQ1}),1.0]])]});}
            var Q18;
            {var subQ0=sQuery(id+"F0.wireOp",EDGE,"E34");var subQ1=sQuery(id+"F0.wireOp",EDGE,"E8");var subQ2=makeQuery(id+"F0.imprint","INTERSECT",VERTEX,{"disambiguationData":[OD(1.0)],"derivedFrom":[subQ1,subQ0]});Q18=makeQuery(id+"F0.imprint","IMPRINT",FACE,{"disambiguationData":[TD([[makeQuery(id+"F0.imprint","IMPRINT",EDGE,{"disambiguationData":[TD([[subQ2,-1.0]])],"derivedFrom":subQ1}),-1.0]])]});}
            var Q19;
            {var subQ0=sQuery(id+"F0.wireOp",EDGE,"E20");var subQ1=sQuery(id+"F0.wireOp",EDGE,"E8");var subQ2=makeQuery(id+"F0.imprint","INTERSECT",VERTEX,{"derivedFrom":[subQ1,subQ0]});Q19=makeQuery(id+"F0.imprint","IMPRINT",FACE,{"disambiguationData":[TD([[makeQuery(id+"F0.imprint","IMPRINT",EDGE,{"disambiguationData":[TD([[subQ2,-1.0]])],"derivedFrom":subQ1}),-1.0]])]});}
            extrude(context, id + "F4", {"entities" : qUnion([Q0, Q1, Q2, Q3, Q4, Q5, Q6, Q7, Q8, Q9, Q10, Q11, Q12, Q13, Q14, Q15, Q16, Q17, Q18, Q19]), "operationType" : NewBodyOperationType.ADD, "depth" : 2.5 * mm});
        }
        {
            var Q0;
            {var subQ0=sQuery(id+"F0.wireOp",EDGE,"E24");var subQ1=sQuery(id+"F0.wireOp",EDGE,"E23");var subQ2=sQuery(id+"F0.wireOp",EDGE,"E20");var subQ3=sQuery(id+"F0.wireOp",EDGE,"E19");var subQ4=sQuery(id+"F0.wireOp",EDGE,"E22");var subQ5=sQuery(id+"F0.wireOp",EDGE,"E21");var subQ6=sQuery(id+"F0.wireOp",EDGE,"E13");var subQ7=sQuery(id+"F0.wireOp",EDGE,"E12");Q0=makeQuery(id+"F4.boolean.opBoolean","MERGE",FACE,{"derivedFrom":[makeQuery(id+"F1.opExtrude","CAP_FACE",FACE,{"disambiguationData":[OSD([sQuery(id+"F0.wireOp",EDGE,"E0"),sQuery(id+"F0.wireOp",EDGE,"E1"),sQuery(id+"F0.wireOp",EDGE,"E8"),sQuery(id+"F0.wireOp",EDGE,"E9"),sQuery(id+"F0.wireOp",EDGE,"E10"),sQuery(id+"F0.wireOp",EDGE,"E11"),subQ7,subQ6,sQuery(id+"F0.wireOp",EDGE,"E15"),sQuery(id+"F0.wireOp",EDGE,"E16"),subQ3,subQ2,subQ5,subQ4,subQ1,subQ0,sQuery(id+"F0.wireOp",EDGE,"E27"),sQuery(id+"F0.wireOp",EDGE,"E28"),sQuery(id+"F0.wireOp",EDGE,"E32"),sQuery(id+"F0.wireOp",EDGE,"E33"),sQuery(id+"F0.wireOp",EDGE,"E37"),sQuery(id+"F0.wireOp",EDGE,"E38")])],"isStart":false}),makeQuery(id+"F4.opExtrude","CAP_FACE",FACE,{"disambiguationData":[OSD([subQ7,subQ6,subQ5,subQ4])],"isStart":false}),makeQuery(id+"F4.opExtrude","CAP_FACE",FACE,{"disambiguationData":[OSD([subQ3,subQ2,subQ1,subQ0])],"isStart":false})]});}
            var sketch = newSketch(context, id + "F5", { "sketchPlane" : qUnion([Q0])});
            skCircle(sketch, "E73", {"center": v(140.86, 10.72) * mm, "radius": 4.05 * mm});
            skCircle(sketch, "E74", {"center": v(107.2, 92.04) * mm, "radius": 4.05 * mm});
            skSolve(sketch);
        }
        {
            var Q0;
            Q0=qSketchRegion(id+"F5",true);
            extrude(context, id + "F6", {"entities" : qUnion([Q0]), "operationType" : NewBodyOperationType.REMOVE, "oppositeDirection" : true, "depth" : 25 * mm});
        }
        {
            var Q0;
            Q0=makeQuery(id+"F0.imprint","IMPRINT",FACE,{"disambiguationData":[TD([[makeQuery(id+"F0.imprint","IMPRINT",EDGE,{"derivedFrom":sQuery(id+"F0.wireOp",EDGE,"E32")}),1.0]])]});
            var Q1;
            Q1=makeQuery(id+"F0.imprint","IMPRINT",FACE,{"disambiguationData":[TD([[makeQuery(id+"F0.imprint","IMPRINT",EDGE,{"derivedFrom":sQuery(id+"F0.wireOp",EDGE,"E33")}),1.0]])]});
            var Q2;
            Q2=makeQuery(id+"F0.imprint","IMPRINT",FACE,{"disambiguationData":[TD([[makeQuery(id+"F0.imprint","IMPRINT",EDGE,{"derivedFrom":sQuery(id+"F0.wireOp",EDGE,"E28")}),1.0]])]});
            var Q3;
            Q3=makeQuery(id+"F0.imprint","IMPRINT",FACE,{"disambiguationData":[TD([[makeQuery(id+"F0.imprint","IMPRINT",EDGE,{"derivedFrom":sQuery(id+"F0.wireOp",EDGE,"E27")}),1.0]])]});
            extrude(context, id + "F7", {"entities" : qUnion([Q0, Q1, Q2, Q3]), "operationType" : NewBodyOperationType.ADD, "depth" : 2.5 * mm});
        }
        {
            var Q0;
            {var subQ0=sQuery(id+"F2.wireOp",EDGE,"E71");var subQ1=makeQuery(id+"F1.opExtrude","CAP_EDGE",EDGE,{"disambiguationData":[OSD([sQuery(id+"F0.wireOp",EDGE,"E22")])],"isStart":false});var subQ2=makeQuery(id+"F2.imprint","INTERSECT",VERTEX,{"derivedFrom":[subQ1,subQ0]});Q0=makeQuery(id+"F2.imprint","IMPRINT",FACE,{"disambiguationData":[TD([[makeQuery(id+"F2.imprint","IMPRINT",EDGE,{"disambiguationData":[TD([[subQ2,-1.0]])],"derivedFrom":subQ0}),1.0]])]});}
            var Q1;
            Q1=makeQuery(id+"F2.imprint","IMPRINT",FACE,{"disambiguationData":[TD([[makeQuery(id+"F2.imprint","IMPRINT",EDGE,{"derivedFrom":makeQuery(id+"F1.opExtrude","CAP_EDGE",EDGE,{"disambiguationData":[OSD([sQuery(id+"F0.wireOp",EDGE,"E28")])],"isStart":false})}),-1.0]])]});
            var Q2;
            Q2=makeQuery(id+"F2.imprint","IMPRINT",FACE,{"disambiguationData":[TD([[makeQuery(id+"F2.imprint","IMPRINT",EDGE,{"derivedFrom":makeQuery(id+"F1.opExtrude","CAP_EDGE",EDGE,{"disambiguationData":[OSD([sQuery(id+"F0.wireOp",EDGE,"E28")])],"isStart":false})}),1.0]])]});
            var Q3;
            {var subQ0=sQuery(id+"F2.wireOp",EDGE,"E62");var subQ3=sQuery(id+"F2.wireOp",EDGE,"E71");var subQ4=makeQuery(id+"F2.imprint","INTERSECT",VERTEX,{"derivedFrom":[subQ0,subQ3]});Q3=makeQuery(id+"F2.imprint","IMPRINT",FACE,{"disambiguationData":[TD([[makeQuery(id+"F2.imprint","IMPRINT",EDGE,{"disambiguationData":[TD([[subQ4,1.0]])],"derivedFrom":subQ3}),1.0]])]});}
            var Q4;
            {var subQ0=sQuery(id+"F2.wireOp",EDGE,"E57");Q4=makeQuery(id+"F2.imprint","IMPRINT",FACE,{"disambiguationData":[TD([[makeQuery(id+"F2.imprint","IMPRINT",EDGE,{"derivedFrom":subQ0}),1.0]])]});}
            var Q5;
            {var subQ5=sQuery(id+"F2.wireOp",EDGE,"E57");Q5=makeQuery(id+"F2.imprint","IMPRINT",FACE,{"disambiguationData":[TD([[makeQuery(id+"F2.imprint","IMPRINT",EDGE,{"derivedFrom":subQ5}),-1.0]])]});}
            var Q6;
            Q6=makeQuery(id+"F2.imprint","IMPRINT",FACE,{"disambiguationData":[TD([[makeQuery(id+"F2.imprint","IMPRINT",EDGE,{"derivedFrom":makeQuery(id+"F1.opExtrude","CAP_EDGE",EDGE,{"disambiguationData":[OSD([sQuery(id+"F0.wireOp",EDGE,"E33")])],"isStart":false})}),1.0]])]});
            extrude(context, id + "F8", {"entities" : qUnion([Q0, Q1, Q2, Q3, Q4, Q5, Q6]), "operationType" : NewBodyOperationType.REMOVE, "oppositeDirection" : true, "depth" : 25 * mm});
        }
        {
            var Q0;
            Q0=makeQuery(id+"F8.boolean.opBoolean","COPY",EDGE,{"derivedFrom":makeQuery(id+"F8.opExtrude","CAP_EDGE",EDGE,{"disambiguationData":[OSD([sQuery(id+"F2.wireOp",EDGE,"E72")])],"isStart":true})});
            var Q1;
            Q1=makeQuery(id+"F8.boolean.opBoolean","COPY",EDGE,{"derivedFrom":makeQuery(id+"F8.opExtrude","CAP_EDGE",EDGE,{"disambiguationData":[OSD([sQuery(id+"F2.wireOp",EDGE,"E71")])],"isStart":true})});
            var Q2;
            {var subQ0=sQuery(id+"F0.wireOp",EDGE,"E33");var subQ1=sQuery(id+"F0.wireOp",EDGE,"E32");var subQ2=sQuery(id+"F0.wireOp",EDGE,"E28");var subQ3=sQuery(id+"F0.wireOp",EDGE,"E27");var subQ4=sQuery(id+"F0.wireOp",EDGE,"E24");var subQ5=sQuery(id+"F0.wireOp",EDGE,"E23");var subQ6=sQuery(id+"F0.wireOp",EDGE,"E20");var subQ7=sQuery(id+"F0.wireOp",EDGE,"E19");var subQ8=sQuery(id+"F0.wireOp",EDGE,"E22");var subQ9=sQuery(id+"F0.wireOp",EDGE,"E21");var subQ10=sQuery(id+"F0.wireOp",EDGE,"E13");var subQ11=sQuery(id+"F0.wireOp",EDGE,"E12");Q2=makeQuery(id+"F8.boolean.opBoolean","INTERSECT",EDGE,{"derivedFrom":[makeQuery(id+"F7.boolean.opBoolean","MERGE",FACE,{"derivedFrom":[makeQuery(id+"F4.boolean.opBoolean","MERGE",FACE,{"derivedFrom":[makeQuery(id+"F1.opExtrude","CAP_FACE",FACE,{"disambiguationData":[OSD([sQuery(id+"F0.wireOp",EDGE,"E0"),sQuery(id+"F0.wireOp",EDGE,"E1"),sQuery(id+"F0.wireOp",EDGE,"E8"),sQuery(id+"F0.wireOp",EDGE,"E9"),sQuery(id+"F0.wireOp",EDGE,"E10"),sQuery(id+"F0.wireOp",EDGE,"E11"),subQ11,subQ10,sQuery(id+"F0.wireOp",EDGE,"E15"),sQuery(id+"F0.wireOp",EDGE,"E16"),subQ7,subQ6,subQ9,subQ8,subQ5,subQ4,subQ3,subQ2,subQ1,subQ0,sQuery(id+"F0.wireOp",EDGE,"E37"),sQuery(id+"F0.wireOp",EDGE,"E38")])],"isStart":true}),makeQuery(id+"F4.opExtrude","CAP_FACE",FACE,{"disambiguationData":[OSD([subQ11,subQ10,subQ9,subQ8])],"isStart":true}),makeQuery(id+"F4.opExtrude","CAP_FACE",FACE,{"disambiguationData":[OSD([subQ7,subQ6,subQ5,subQ4])],"isStart":true})]}),makeQuery(id+"F7.opExtrude","CAP_FACE",FACE,{"disambiguationData":[OSD([subQ3])],"isStart":true}),makeQuery(id+"F7.opExtrude","CAP_FACE",FACE,{"disambiguationData":[OSD([subQ2])],"isStart":true}),makeQuery(id+"F7.opExtrude","CAP_FACE",FACE,{"disambiguationData":[OSD([subQ1])],"isStart":true}),makeQuery(id+"F7.opExtrude","CAP_FACE",FACE,{"disambiguationData":[OSD([subQ0])],"isStart":true})]}),makeQuery(id+"F8.opExtrude","SWEPT_FACE",FACE,{"disambiguationData":[OSD([sQuery(id+"F2.wireOp",EDGE,"E71")])]})]});}
            var Q3;
            {var subQ0=sQuery(id+"F0.wireOp",EDGE,"E33");var subQ1=sQuery(id+"F0.wireOp",EDGE,"E32");var subQ2=sQuery(id+"F0.wireOp",EDGE,"E28");var subQ3=sQuery(id+"F0.wireOp",EDGE,"E27");var subQ4=sQuery(id+"F0.wireOp",EDGE,"E24");var subQ5=sQuery(id+"F0.wireOp",EDGE,"E23");var subQ6=sQuery(id+"F0.wireOp",EDGE,"E20");var subQ7=sQuery(id+"F0.wireOp",EDGE,"E19");var subQ8=sQuery(id+"F0.wireOp",EDGE,"E22");var subQ9=sQuery(id+"F0.wireOp",EDGE,"E21");var subQ10=sQuery(id+"F0.wireOp",EDGE,"E13");var subQ11=sQuery(id+"F0.wireOp",EDGE,"E12");Q3=makeQuery(id+"F8.boolean.opBoolean","INTERSECT",EDGE,{"derivedFrom":[makeQuery(id+"F7.boolean.opBoolean","MERGE",FACE,{"derivedFrom":[makeQuery(id+"F4.boolean.opBoolean","MERGE",FACE,{"derivedFrom":[makeQuery(id+"F1.opExtrude","CAP_FACE",FACE,{"disambiguationData":[OSD([sQuery(id+"F0.wireOp",EDGE,"E0"),sQuery(id+"F0.wireOp",EDGE,"E1"),sQuery(id+"F0.wireOp",EDGE,"E8"),sQuery(id+"F0.wireOp",EDGE,"E9"),sQuery(id+"F0.wireOp",EDGE,"E10"),sQuery(id+"F0.wireOp",EDGE,"E11"),subQ11,subQ10,sQuery(id+"F0.wireOp",EDGE,"E15"),sQuery(id+"F0.wireOp",EDGE,"E16"),subQ7,subQ6,subQ9,subQ8,subQ5,subQ4,subQ3,subQ2,subQ1,subQ0,sQuery(id+"F0.wireOp",EDGE,"E37"),sQuery(id+"F0.wireOp",EDGE,"E38")])],"isStart":true}),makeQuery(id+"F4.opExtrude","CAP_FACE",FACE,{"disambiguationData":[OSD([subQ11,subQ10,subQ9,subQ8])],"isStart":true}),makeQuery(id+"F4.opExtrude","CAP_FACE",FACE,{"disambiguationData":[OSD([subQ7,subQ6,subQ5,subQ4])],"isStart":true})]}),makeQuery(id+"F7.opExtrude","CAP_FACE",FACE,{"disambiguationData":[OSD([subQ3])],"isStart":true}),makeQuery(id+"F7.opExtrude","CAP_FACE",FACE,{"disambiguationData":[OSD([subQ2])],"isStart":true}),makeQuery(id+"F7.opExtrude","CAP_FACE",FACE,{"disambiguationData":[OSD([subQ1])],"isStart":true}),makeQuery(id+"F7.opExtrude","CAP_FACE",FACE,{"disambiguationData":[OSD([subQ0])],"isStart":true})]}),makeQuery(id+"F8.opExtrude","SWEPT_FACE",FACE,{"disambiguationData":[OSD([sQuery(id+"F2.wireOp",EDGE,"E72")])]})]});}
            fillet(context, id + "F9", {"entities" : qUnion([Q0, Q1, Q2, Q3]), "radius" : 1 * mm, "tangentPropagation" : true, "allowEdgeOverflow" : false});
        }
        {
            var Q0;
            Q0=makeQuery(id+"F2.imprint","IMPRINT",FACE,{"disambiguationData":[TD([[makeQuery(id+"F2.imprint","IMPRINT",EDGE,{"derivedFrom":sQuery(id+"F2.wireOp",EDGE,"E43")}),-1.0]])]});
            var sketch = newSketch(context, id + "F10", { "sketchPlane" : qUnion([Q0])});
            skCircle(sketch, "E75", {"center": v(130.21, 32.35) * mm, "radius": 1.5 * mm});
            skCircle(sketch, "E76", {"center": v(145.71, 35.4) * mm, "radius": 1.5 * mm});
            skCircle(sketch, "E77", {"center": v(128.1, 78.07) * mm, "radius": 1.5 * mm});
            skCircle(sketch, "E78", {"center": v(114.87, 69.32) * mm, "radius": 1.5 * mm});
            skSolve(sketch);
        }
        {
            var Q0;
            Q0=qSketchRegion(id+"F10",true);
            extrude(context, id + "F11", {"entities" : qUnion([Q0]), "operationType" : NewBodyOperationType.REMOVE, "oppositeDirection" : true, "depth" : 25 * mm});
        }
        {
            var Q0;
            Q0=makeQuery(id+"F2.imprint","IMPRINT",FACE,{"disambiguationData":[TD([[makeQuery(id+"F2.imprint","IMPRINT",EDGE,{"derivedFrom":sQuery(id+"F2.wireOp",EDGE,"E43")}),-1.0]])]});
            var sketch = newSketch(context, id + "F12", { "sketchPlane" : qUnion([Q0])});
            skCircle(sketch, "E79", {"center": v(107.2, 92.04) * mm, "radius": 4.05 * mm});
            skCircle(sketch, "E80", {"center": v(107.2, 92.04) * mm, "radius": 1.5 * mm});
            skSolve(sketch);
        }
        {
            var Q0;
            Q0=qSketchRegion(id+"F12",true);
            extrude(context, id + "F13", {"entities" : qUnion([Q0]), "operationType" : NewBodyOperationType.ADD, "oppositeDirection" : true, "depth" : 2.5 * mm});
        }
        {
            var Q0;
            Q0=makeQuery(id+"F1.opExtrude","CAP_EDGE",EDGE,{"disambiguationData":[OSD([sQuery(id+"F0.wireOp",EDGE,"E38")])],"isStart":false});
            var Q1;
            Q1=makeQuery(id+"F1.opExtrude","CAP_EDGE",EDGE,{"disambiguationData":[OSD([sQuery(id+"F0.wireOp",EDGE,"E10"),sQuery(id+"F0.wireOp",EDGE,"E11")])],"isStart":false});
            var Q2;
            Q2=makeQuery(id+"F1.opExtrude","CAP_EDGE",EDGE,{"disambiguationData":[OSD([sQuery(id+"F0.wireOp",EDGE,"E0")])],"isStart":false});
            var Q3;
            Q3=makeQuery(id+"F3.boolean.opBoolean","COPY",EDGE,{"derivedFrom":makeQuery(id+"F3.opExtrude","CAP_EDGE",EDGE,{"disambiguationData":[OSD([sQuery(id+"F2.wireOp",EDGE,"E42")])],"isStart":true})});
            var Q4;
            Q4=makeQuery(id+"F3.boolean.opBoolean","COPY",EDGE,{"derivedFrom":makeQuery(id+"F3.opExtrude","CAP_EDGE",EDGE,{"disambiguationData":[OSD([sQuery(id+"F2.wireOp",EDGE,"E43")])],"isStart":true})});
            var Q5;
            Q5=makeQuery(id+"F3.boolean.opBoolean","COPY",EDGE,{"derivedFrom":makeQuery(id+"F3.opExtrude","CAP_EDGE",EDGE,{"disambiguationData":[OSD([sQuery(id+"F2.wireOp",EDGE,"E44")])],"isStart":true})});
            var Q6;
            Q6=makeQuery(id+"F1.opExtrude","CAP_EDGE",EDGE,{"disambiguationData":[OSD([sQuery(id+"F0.wireOp",EDGE,"E15"),sQuery(id+"F0.wireOp",EDGE,"E16")])],"isStart":false});
            var Q7;
            Q7=makeQuery(id+"F1.opExtrude","CAP_EDGE",EDGE,{"disambiguationData":[OSD([sQuery(id+"F0.wireOp",EDGE,"E37")])],"isStart":false});
            var Q8;
            Q8=makeQuery(id+"F1.opExtrude","CAP_EDGE",EDGE,{"disambiguationData":[OSD([sQuery(id+"F0.wireOp",EDGE,"E8")])],"isStart":true});
            var Q9;
            Q9=makeQuery(id+"F1.opExtrude","CAP_EDGE",EDGE,{"disambiguationData":[OSD([sQuery(id+"F0.wireOp",EDGE,"E37")])],"isStart":true});
            var Q10;
            Q10=makeQuery(id+"F1.opExtrude","CAP_EDGE",EDGE,{"disambiguationData":[OSD([sQuery(id+"F0.wireOp",EDGE,"E15"),sQuery(id+"F0.wireOp",EDGE,"E16")])],"isStart":true});
            var Q11;
            Q11=makeQuery(id+"F1.opExtrude","CAP_EDGE",EDGE,{"disambiguationData":[OSD([sQuery(id+"F0.wireOp",EDGE,"E38")])],"isStart":true});
            var Q12;
            Q12=makeQuery(id+"F1.opExtrude","CAP_EDGE",EDGE,{"disambiguationData":[OSD([sQuery(id+"F0.wireOp",EDGE,"E10"),sQuery(id+"F0.wireOp",EDGE,"E11")])],"isStart":true});
            var Q13;
            Q13=makeQuery(id+"F3.boolean.opBoolean","INTERSECT",EDGE,{"derivedFrom":[makeQuery(id+"F1.opExtrude","CAP_FACE",FACE,{"disambiguationData":[OSD([sQuery(id+"F0.wireOp",EDGE,"E0"),sQuery(id+"F0.wireOp",EDGE,"E1"),sQuery(id+"F0.wireOp",EDGE,"E8"),sQuery(id+"F0.wireOp",EDGE,"E9"),sQuery(id+"F0.wireOp",EDGE,"E10"),sQuery(id+"F0.wireOp",EDGE,"E11"),sQuery(id+"F0.wireOp",EDGE,"E12"),sQuery(id+"F0.wireOp",EDGE,"E13"),sQuery(id+"F0.wireOp",EDGE,"E15"),sQuery(id+"F0.wireOp",EDGE,"E16"),sQuery(id+"F0.wireOp",EDGE,"E19"),sQuery(id+"F0.wireOp",EDGE,"E20"),sQuery(id+"F0.wireOp",EDGE,"E21"),sQuery(id+"F0.wireOp",EDGE,"E22"),sQuery(id+"F0.wireOp",EDGE,"E23"),sQuery(id+"F0.wireOp",EDGE,"E24"),sQuery(id+"F0.wireOp",EDGE,"E27"),sQuery(id+"F0.wireOp",EDGE,"E28"),sQuery(id+"F0.wireOp",EDGE,"E32"),sQuery(id+"F0.wireOp",EDGE,"E33"),sQuery(id+"F0.wireOp",EDGE,"E37"),sQuery(id+"F0.wireOp",EDGE,"E38"),sQuery(id+"F0.wireOp",EDGE,"E41")])],"isStart":true}),makeQuery(id+"F3.opExtrude","SWEPT_FACE",FACE,{"disambiguationData":[OSD([sQuery(id+"F2.wireOp",EDGE,"E43")])]})]});
            var Q14;
            Q14=makeQuery(id+"F3.boolean.opBoolean","INTERSECT",EDGE,{"derivedFrom":[makeQuery(id+"F1.opExtrude","CAP_FACE",FACE,{"disambiguationData":[OSD([sQuery(id+"F0.wireOp",EDGE,"E0"),sQuery(id+"F0.wireOp",EDGE,"E1"),sQuery(id+"F0.wireOp",EDGE,"E8"),sQuery(id+"F0.wireOp",EDGE,"E9"),sQuery(id+"F0.wireOp",EDGE,"E10"),sQuery(id+"F0.wireOp",EDGE,"E11"),sQuery(id+"F0.wireOp",EDGE,"E12"),sQuery(id+"F0.wireOp",EDGE,"E13"),sQuery(id+"F0.wireOp",EDGE,"E15"),sQuery(id+"F0.wireOp",EDGE,"E16"),sQuery(id+"F0.wireOp",EDGE,"E19"),sQuery(id+"F0.wireOp",EDGE,"E20"),sQuery(id+"F0.wireOp",EDGE,"E21"),sQuery(id+"F0.wireOp",EDGE,"E22"),sQuery(id+"F0.wireOp",EDGE,"E23"),sQuery(id+"F0.wireOp",EDGE,"E24"),sQuery(id+"F0.wireOp",EDGE,"E27"),sQuery(id+"F0.wireOp",EDGE,"E28"),sQuery(id+"F0.wireOp",EDGE,"E32"),sQuery(id+"F0.wireOp",EDGE,"E33"),sQuery(id+"F0.wireOp",EDGE,"E37"),sQuery(id+"F0.wireOp",EDGE,"E38"),sQuery(id+"F0.wireOp",EDGE,"E41")])],"isStart":true}),makeQuery(id+"F3.opExtrude","SWEPT_FACE",FACE,{"disambiguationData":[OSD([sQuery(id+"F2.wireOp",EDGE,"E44")])]})]});
            var Q15;
            Q15=makeQuery(id+"F3.boolean.opBoolean","INTERSECT",EDGE,{"derivedFrom":[makeQuery(id+"F1.opExtrude","CAP_FACE",FACE,{"disambiguationData":[OSD([sQuery(id+"F0.wireOp",EDGE,"E0"),sQuery(id+"F0.wireOp",EDGE,"E1"),sQuery(id+"F0.wireOp",EDGE,"E8"),sQuery(id+"F0.wireOp",EDGE,"E9"),sQuery(id+"F0.wireOp",EDGE,"E10"),sQuery(id+"F0.wireOp",EDGE,"E11"),sQuery(id+"F0.wireOp",EDGE,"E12"),sQuery(id+"F0.wireOp",EDGE,"E13"),sQuery(id+"F0.wireOp",EDGE,"E15"),sQuery(id+"F0.wireOp",EDGE,"E16"),sQuery(id+"F0.wireOp",EDGE,"E19"),sQuery(id+"F0.wireOp",EDGE,"E20"),sQuery(id+"F0.wireOp",EDGE,"E21"),sQuery(id+"F0.wireOp",EDGE,"E22"),sQuery(id+"F0.wireOp",EDGE,"E23"),sQuery(id+"F0.wireOp",EDGE,"E24"),sQuery(id+"F0.wireOp",EDGE,"E27"),sQuery(id+"F0.wireOp",EDGE,"E28"),sQuery(id+"F0.wireOp",EDGE,"E32"),sQuery(id+"F0.wireOp",EDGE,"E33"),sQuery(id+"F0.wireOp",EDGE,"E37"),sQuery(id+"F0.wireOp",EDGE,"E38"),sQuery(id+"F0.wireOp",EDGE,"E41")])],"isStart":true}),makeQuery(id+"F3.opExtrude","SWEPT_FACE",FACE,{"disambiguationData":[OSD([sQuery(id+"F2.wireOp",EDGE,"E42")])]})]});
            fillet(context, id + "F14", {"entities" : qUnion([Q0, Q1, Q2, Q3, Q4, Q5, Q6, Q7, Q8, Q9, Q10, Q11, Q12, Q13, Q14, Q15]), "radius" : 1 * mm, "tangentPropagation" : true, "allowEdgeOverflow" : false});
        }
    });
